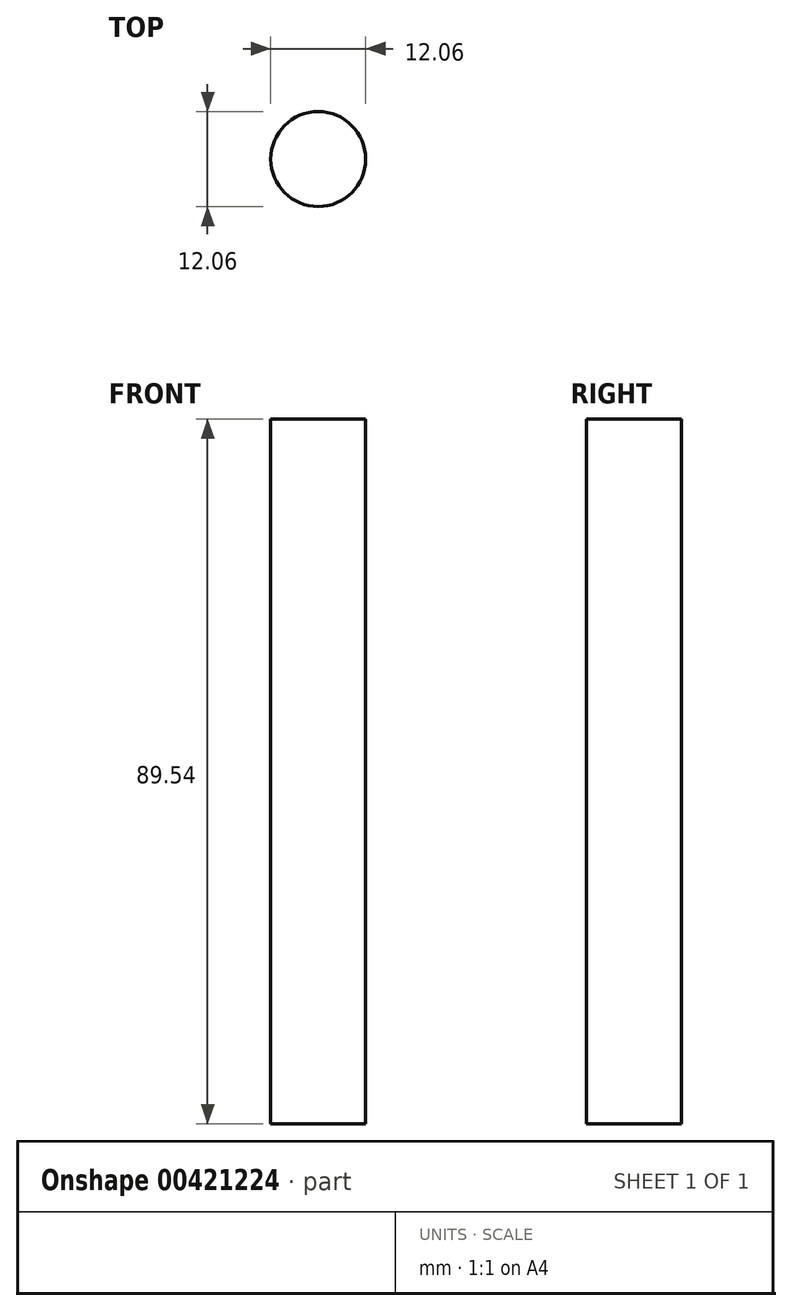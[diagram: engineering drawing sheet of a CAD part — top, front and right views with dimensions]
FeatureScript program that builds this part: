
annotation { "Feature Type Name" : "Feature", "Feature Type Description" : "" }
export const myFeature = defineFeature(function(context is Context, id is Id, definition is map)
    precondition{}
    {
        {
            var Q0;
            Q0=qCreatedBy(makeId("Top.planeOp"),FACE);
            var sketch = newSketch(context, id + "F0", { "sketchPlane" : qUnion([Q0])});
            skCircle(sketch, "E0", {"center": v(0, 0) * mm, "radius": 6.03 * mm});
            skSolve(sketch);
        }
        {
            var Q0;
            Q0 = qSketchRegion(id + "F0", true);
            extrude(context, id + "F1", {"entities" : qUnion([Q0]), "depth" : 89.53 * mm});
        }
    });
